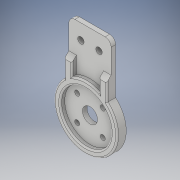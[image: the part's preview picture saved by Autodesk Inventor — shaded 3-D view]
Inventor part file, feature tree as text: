
AUTODESK INVENTOR PART (.ipt)
format: ipt  version: 2018 (Build 220112000, 112)  size: 222,720 bytes
history: native  units: in
note: dims shown in document units (in); Inventor stores cm internally (conversion verified against a paired STEP export)
features: extrude x4, sketch x4, projected_geometry x3, fillet x2, chamfer x1
ambient origin geometry x8: Origin, YZ Plane, XZ Plane, XY Plane, X Axis, Y Axis, Z Axis, Center Point
bodies: Solid1 (feature_tree)
feature tree (14):
  extrude  "Extrusion1"  Depth=1.9685in
  extrude  "Extrusion2"  Depth=1.1024in
  extrude  "Extrusion3"  Depth=0.7874in
  chamfer  "Chamfer1"  Distance=0.1969in
  fillet  "Fillet1"  Radius=0.1181in
  extrude  "Extrusion4"  Depth=0.3937in
  fillet  "Fillet2"  Radius=0.1654in
  sketch  "Sketch1"  dims[d0=1.6535in d1=1.9685in]
  sketch  "Sketch2"  dims[d2=0.1181in d3=0.0in d4=1.1024in]
  projected_geometry  "Projected Loop1"
  sketch  "Sketch3"  dims[d5=1.3189in d6=0.7874in]
  projected_geometry  "Projected Loop2"
  projected_geometry  "Projected Loop3"
  sketch  "Sketch4"  dims[d7=0.1969in d8=0.1969in d9=0.1181in d10=0.0in d11=0.3937in d12=0.1654in d13=0.4724in d14=0.3937in d15=0.1181in d16=0.0in d17=0.1181in d18=0.0787in d19=45.0deg d20=0.0394in d21=45.0deg d22=0.1299in d23=0.4724in d24=1.5748in d26=360.0deg d28=0.1181in d29=0.0in d30=0.1575in]
